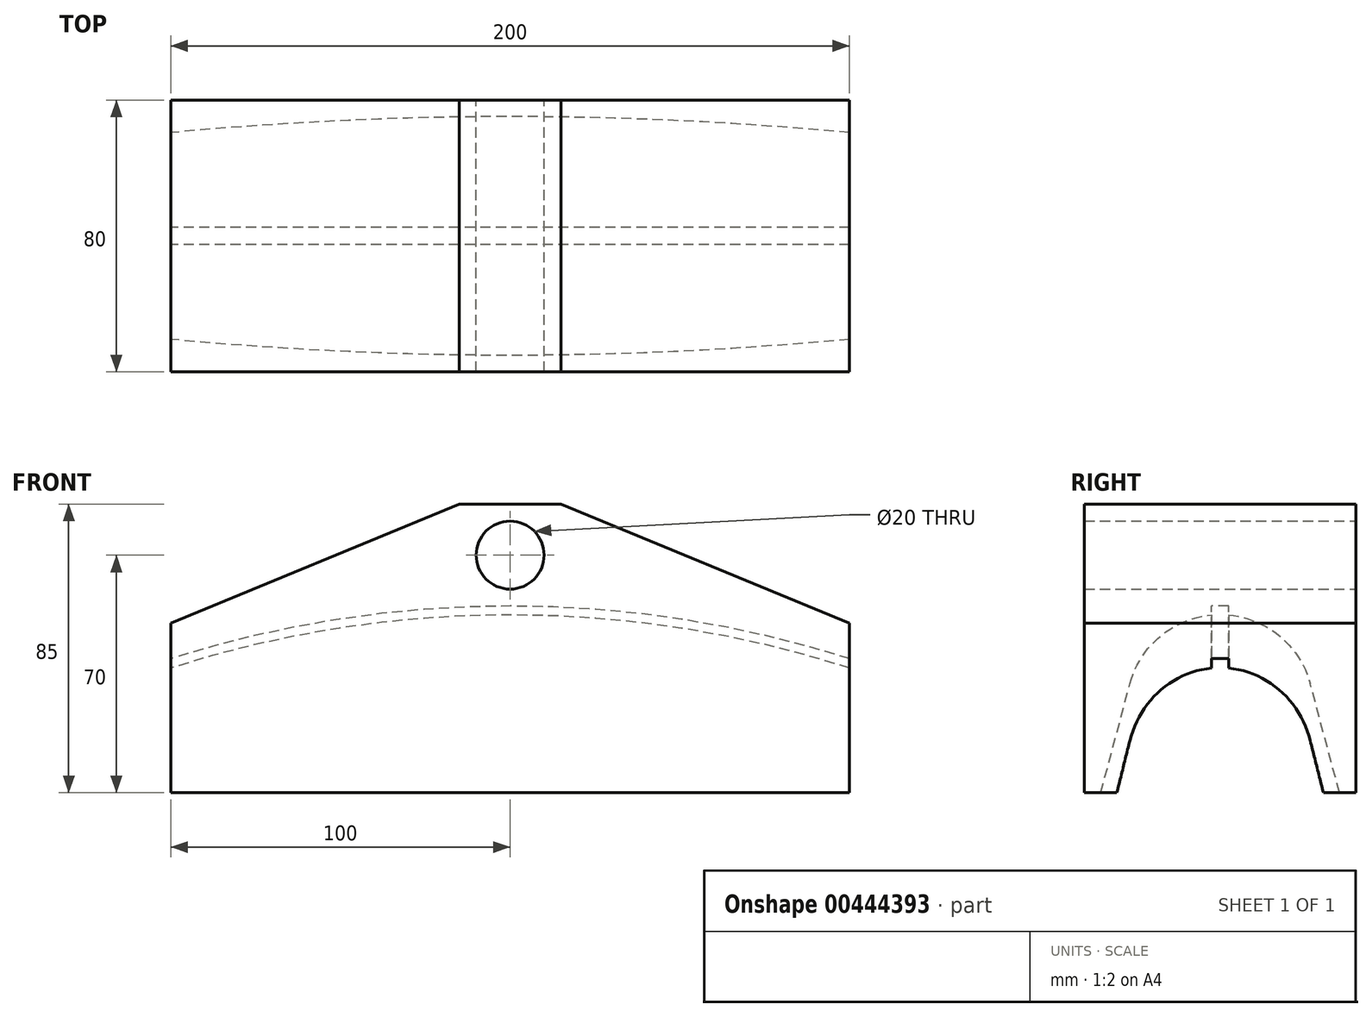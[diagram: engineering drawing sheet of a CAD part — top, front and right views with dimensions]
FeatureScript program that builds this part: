
annotation { "Feature Type Name" : "Feature", "Feature Type Description" : "" }
export const myFeature = defineFeature(function(context is Context, id is Id, definition is map)
    precondition{}
    {
        {
            var Q0;
            Q0=qCreatedBy(makeId("Front.planeOp"),FACE);
            var sketch = newSketch(context, id + "F0", { "sketchPlane" : qUnion([Q0])});
            skCircle(sketch, "E0", {"center": v(0, 0) * mm, "radius": 300 * mm, "construction": true});
            skLineSegment(sketch, "E1", {"start": v(0, 0) * mm, "end": v(0, 345) * mm, "construction": true});
            skCircle(sketch, "E2", {"center": v(0, 345) * mm, "radius": 10 * mm});
            skCircle(sketch, "E3", {"center": v(0, 0) * mm, "radius": 325 * mm, "construction": true});
            skPoint(sketch, "E4", {"position": v(0, 325) * mm});
            skPoint(sketch, "E5", {"position": v(0, 335) * mm});
            skLineSegment(sketch, "E6", {"start": v(-15, 360) * mm, "end": v(0, 360) * mm});
            skLineSegment(sketch, "E7", {"start": v(0, 345) * mm, "end": v(0, 360) * mm, "construction": true});
            skLineSegment(sketch, "E8", {"start": v(-100, 325) * mm, "end": v(-100, 275) * mm});
            skLineSegment(sketch, "E9", {"start": v(-100, 275) * mm, "end": v(0, 275) * mm});
            skLineSegment(sketch, "E10", {"start": v(-15, 360) * mm, "end": v(-100, 325) * mm});
            skLineSegment(sketch, "E11.MirrorCS", {"start": v(15, 360) * mm, "end": v(0, 360) * mm});
            skLineSegment(sketch, "E12.MirrorCS", {"start": v(15, 360) * mm, "end": v(100, 325) * mm});
            skLineSegment(sketch, "E13.MirrorCS", {"start": v(100, 325) * mm, "end": v(100, 275) * mm});
            skLineSegment(sketch, "E14.MirrorCS", {"start": v(100, 275) * mm, "end": v(0, 275) * mm});
            skSolve(sketch);
        }
        {
            var Q0;
            Q0=makeQuery(id+"F0.imprint","IMPRINT",FACE,{"disambiguationData":[TD([[makeQuery(id+"F0.imprint","IMPRINT",EDGE,{"derivedFrom":sQuery(id+"F0.wireOp",EDGE,"E2")}),-1.0]])]});
            extrude(context, id + "F1", {"entities" : qUnion([Q0]), "endBound" : BoundingType.SYMMETRIC, "depth" : 80 * mm});
        }
        {
            var Q0;
            Q0=qCreatedBy(makeId("Right.planeOp"),FACE);
            var sketch = newSketch(context, id + "F2", { "sketchPlane" : qUnion([Q0])});
            skArc(sketch, "E15", {"start": v(26.56, 307.12) * mm, "mid": v(17.72, 321.03) * mm, "end": v(2.5, 327.39) * mm});
            skLineSegment(sketch, "E16", {"start": v(0, 300) * mm, "end": v(0, 260) * mm, "construction": true});
            skLineSegment(sketch, "E17", {"start": v(39.19, 260) * mm, "end": v(-39.19, 260) * mm});
            skLineSegment(sketch, "E18", {"start": v(26.56, 307.12) * mm, "end": v(39.19, 260) * mm});
            skLineSegment(sketch, "E19", {"start": v(-26.56, 307.12) * mm, "end": v(-39.19, 260) * mm});
            skLineSegment(sketch, "E20", {"start": v(-2.5, 327.39) * mm, "end": v(-2.5, 330) * mm});
            skLineSegment(sketch, "E21", {"start": v(-2.5, 330) * mm, "end": v(2.5, 330) * mm});
            skLineSegment(sketch, "E22", {"start": v(2.5, 330) * mm, "end": v(2.5, 327.39) * mm});
            skArc(sketch, "E23.trimOffspring", {"start": v(-2.5, 327.39) * mm, "mid": v(-17.72, 321.03) * mm, "end": v(-26.56, 307.12) * mm});
            skLineSegment(sketch, "E24", {"start": v(0, 0) * mm, "end": v(-60.92, 0) * mm, "construction": true});
            skSolve(sketch);
        }
        {
            var Q0;
            Q0=qSketchRegion(id+"F2",true);
            var Q1;
            Q1=sQuery(id+"F0.wireOp",EDGE,"E0");
            revolve(context, id + "F3", {"operationType" : NewBodyOperationType.REMOVE, "entities" : qUnion([Q0]), "axis" : qUnion([Q1]), "revolveType" : RevolveType.FULL, "oppositeDirection" : true});
        }
    });
